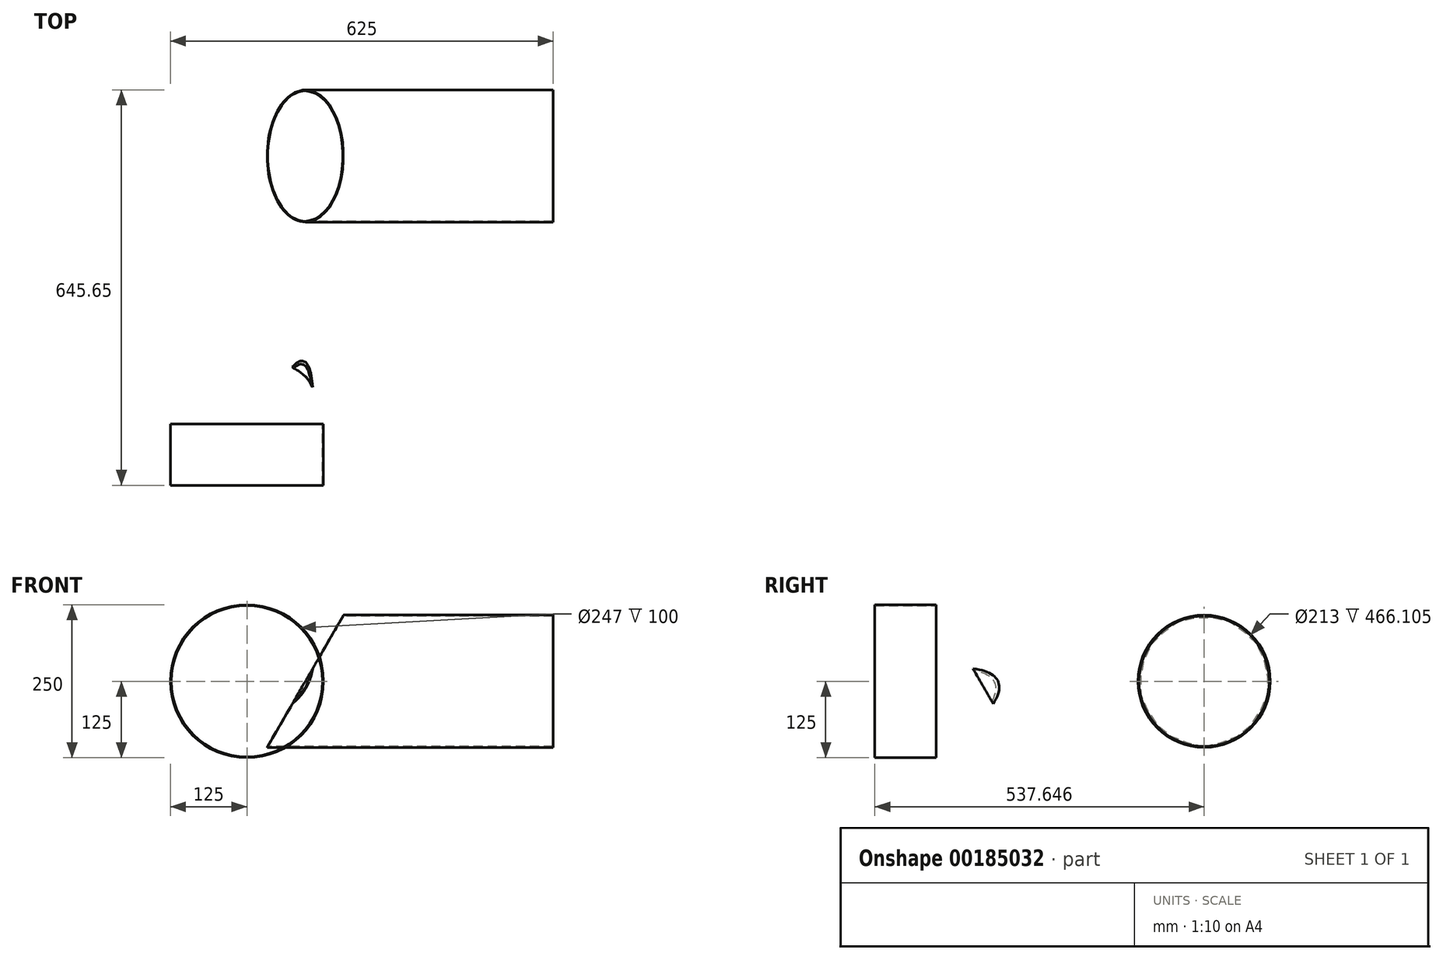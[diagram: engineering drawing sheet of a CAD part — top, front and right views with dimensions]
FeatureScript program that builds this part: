
annotation { "Feature Type Name" : "Feature", "Feature Type Description" : "" }
export const myFeature = defineFeature(function(context is Context, id is Id, definition is map)
    precondition{}
    {
        {
            var Q0;
            Q0=qCreatedBy(makeId("Front.planeOp"),FACE);
            var sketch = newSketch(context, id + "F0", { "sketchPlane" : qUnion([Q0])});
            skCircle(sketch, "E0", {"center": v(0, 0) * mm, "radius": 125 * mm});
            skCircle(sketch, "E1", {"center": v(0, 0) * mm, "radius": 123.5 * mm});
            skSolve(sketch);
        }
        {
            var Q0;
            Q0 = qSketchRegion(id + "F0", true);
            extrude(context, id + "F1", {"entities" : qUnion([Q0]), "depth" : 100 * mm, "offsetDistance" : 25 * mm});
        }
        {
            var Q0;
            Q0=qCreatedBy(makeId("Right.planeOp"),FACE);
            var sketch = newSketch(context, id + "F2", { "sketchPlane" : qUnion([Q0])});
            skLineSegment(sketch, "E2", {"start": v(0, 0) * mm, "end": v(97.3, 56.18) * mm});
            skLineSegment(sketch, "E3", {"start": v(0, 124.7) * mm, "end": v(43.3, 149.7) * mm});
            skLineSegment(sketch, "E4", {"start": v(151.3, -37.35) * mm, "end": v(0, -124.7) * mm});
            skLineSegment(sketch, "E5", {"start": v(0, 124.7) * mm, "end": v(108, -62.35) * mm, "construction": true});
            skLineSegment(sketch, "E6", {"start": v(43.3, 149.7) * mm, "end": v(151.3, -37.35) * mm, "construction": true});
            skLineSegment(sketch, "E7", {"start": v(0, 124.7) * mm, "end": v(0.75, 123.4) * mm});
            skLineSegment(sketch, "E8", {"start": v(0.75, 123.4) * mm, "end": v(44.05, 148.4) * mm});
            skLineSegment(sketch, "E9", {"start": v(44.05, 148.4) * mm, "end": v(43.3, 149.7) * mm});
            skSolve(sketch);
        }
        {
            var Q0;
            Q0 = qSketchRegion(id + "F2", true);
            var Q1;
            Q1=sQuery(id+"F2.wireOp",EDGE,"E2");
            revolve(context, id + "F3", {"surfaceOperationType" : NewSurfaceOperationType.NEW, "entities" : qUnion([Q0]), "axis" : qUnion([Q1]), "revolveType" : RevolveType.FULL});
        }
        {
            var Q0;
            Q0 = qSketchRegion(id + "F2", true);
            extrude(context, id + "F4", {"entities" : qUnion([Q0]), "operationType" : NewBodyOperationType.ADD, "depth" : 25 * mm, "offsetDistance" : 25 * mm});
        }
        {
            var Q0;
            Q0=qCreatedBy(makeId("Right.planeOp"),FACE);
            var sketch = newSketch(context, id + "F5", { "sketchPlane" : qUnion([Q0])});
            skCircle(sketch, "E10", {"center": v(437.65, 0) * mm, "radius": 106.5 * mm});
            skCircle(sketch, "E11", {"center": v(437.65, 0) * mm, "radius": 108 * mm});
            skSolve(sketch);
        }
        {
            var Q0;
            Q0 = qSketchRegion(id + "F5", true);
            extrude(context, id + "F6", {"entities" : qUnion([Q0]), "depth" : 500 * mm, "offsetDistance" : 25 * mm});
        }
        {
            var Q0;
            Q0=qCreatedBy(makeId("Front.planeOp"),FACE);
            var sketch = newSketch(context, id + "F7", { "sketchPlane" : qUnion([Q0])});
            skLineSegment(sketch, "E12", {"start": v(0, -165.26) * mm, "end": v(209.28, 197.22) * mm});
            skLineSegment(sketch, "E13", {"start": v(209.28, 197.22) * mm, "end": v(-95.7, 373.3) * mm});
            skLineSegment(sketch, "E14", {"start": v(-95.7, 373.3) * mm, "end": v(-296.16, 26.12) * mm});
            skLineSegment(sketch, "E15", {"start": v(-296.16, 26.12) * mm, "end": v(8.83, -149.97) * mm});
            skSolve(sketch);
        }
        {
            var Q0;
            Q0 = qSketchRegion(id + "F7", true);
            extrude(context, id + "F8", {"entities" : qUnion([Q0]), "operationType" : NewBodyOperationType.REMOVE, "oppositeDirection" : true, "depth" : 600 * mm, "offsetDistance" : 25 * mm});
        }
    });
